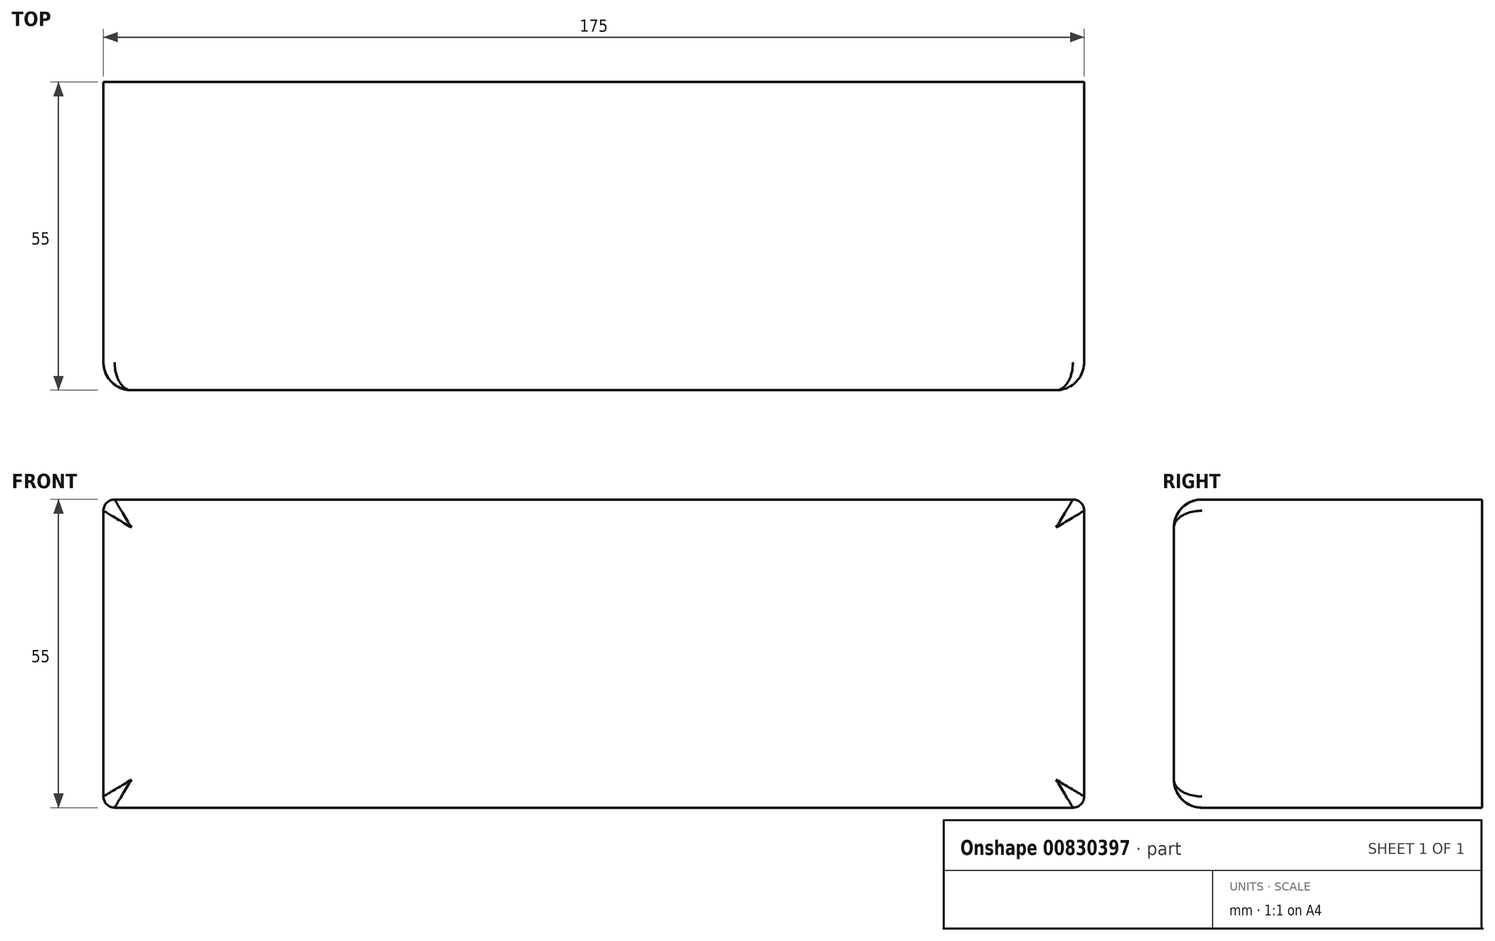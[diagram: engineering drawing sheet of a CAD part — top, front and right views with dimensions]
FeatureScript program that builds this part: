
annotation { "Feature Type Name" : "Feature", "Feature Type Description" : "" }
export const myFeature = defineFeature(function(context is Context, id is Id, definition is map)
    precondition{}
    {
        {
            var Q0;
            Q0=qCreatedBy(makeId("Front.planeOp"),FACE);
            var sketch = newSketch(context, id + "F0", { "sketchPlane" : qUnion([Q0])});
            skLineSegment(sketch, "E0.bottom", {"start": v(-82.2, 50.75) * mm, "end": v(88.8, 50.75) * mm});
            skLineSegment(sketch, "E0.top", {"start": v(-82.2, -4.25) * mm, "end": v(88.8, -4.25) * mm});
            skLineSegment(sketch, "E0.left", {"start": v(-84.2, 48.75) * mm, "end": v(-84.2, -2.25) * mm});
            skLineSegment(sketch, "E0.right", {"start": v(90.8, 48.75) * mm, "end": v(90.8, -2.25) * mm});
            skPoint(sketch, "E1.visualSharp", {"position": v(-84.2, 50.75) * mm});
            skArc(sketch, "E1.filletArc", {"start": v(-82.2, 50.75) * mm, "mid": v(-83.6, 50.16) * mm, "end": v(-84.2, 48.75) * mm});
            skPoint(sketch, "E2.visualSharp", {"position": v(-84.2, -4.25) * mm});
            skArc(sketch, "E2.filletArc", {"start": v(-84.2, -2.25) * mm, "mid": v(-83.6, -3.67) * mm, "end": v(-82.2, -4.25) * mm});
            skPoint(sketch, "E3.visualSharp", {"position": v(90.8, 50.75) * mm});
            skArc(sketch, "E3.filletArc", {"start": v(90.8, 48.75) * mm, "mid": v(90.22, 50.16) * mm, "end": v(88.8, 50.75) * mm});
            skPoint(sketch, "E4.visualSharp", {"position": v(90.8, -4.25) * mm});
            skArc(sketch, "E4.filletArc", {"start": v(88.8, -4.25) * mm, "mid": v(90.22, -3.67) * mm, "end": v(90.8, -2.25) * mm});
            skSolve(sketch);
        }
        {
            var Q0;
            Q0 = qSketchRegion(id + "F0", true);
            var Q1;
            Q1 = qSketchRegion(id + "F46LLDhD2o69u39_1", true);
            extrude(context, id + "F1", {"entities" : qUnion([Q0, Q1]), "depth" : 55 * mm, "offsetDistance" : 25 * mm});
        }
        {
            var Q0;
            Q0=makeQuery(id+"F1.opExtrude","SWEPT_EDGE",EDGE,{"disambiguationData":[OSD([sQuery(id+"F0.wireOp",EDGE,"E0.bottom"),sQuery(id+"F0.wireOp",EDGE,"E3.filletArc")])]});
            var Q1;
            Q1=makeQuery(id+"F1.opExtrude","CAP_EDGE",EDGE,{"disambiguationData":[OSD([sQuery(id+"F0.wireOp",EDGE,"E0.right")])],"isStart":false});
            fillet(context, id + "F2", {"entities" : qUnion([Q0, Q1]), "radius" : 5 * mm, "tangentPropagation" : true, "allowEdgeOverflow" : false});
        }
        {
            var Q0;
            Q0=makeQuery(id+"F1.opExtrude","CAP_FACE",FACE,{"disambiguationData":[OSD([sQuery(id+"F0.wireOp",EDGE,"E0.bottom"),sQuery(id+"F0.wireOp",EDGE,"E0.top"),sQuery(id+"F0.wireOp",EDGE,"E0.left"),sQuery(id+"F0.wireOp",EDGE,"E0.right"),sQuery(id+"F0.wireOp",EDGE,"E1.filletArc"),sQuery(id+"F0.wireOp",EDGE,"E2.filletArc"),sQuery(id+"F0.wireOp",EDGE,"E3.filletArc"),sQuery(id+"F0.wireOp",EDGE,"E4.filletArc")])],"isStart":true});
            var sketch = newSketch(context, id + "F3", { "sketchPlane" : qUnion([Q0])});
            skLineSegment(sketch, "E5.bottom", {"start": v(-85.8, 45.75) * mm, "end": v(79.2, 45.75) * mm});
            skLineSegment(sketch, "E5.top", {"start": v(-85.8, 0.75) * mm, "end": v(79.2, 0.75) * mm});
            skLineSegment(sketch, "E5.left", {"start": v(-85.8, 45.75) * mm, "end": v(-85.8, 0.75) * mm});
            skLineSegment(sketch, "E5.right", {"start": v(79.2, 45.75) * mm, "end": v(79.2, 0.75) * mm});
            skSolve(sketch);
        }
        {
            var Q0;
            Q0=makeQuery(id+"F3.imprint","IMPRINT",FACE,{"disambiguationData":[TD([[makeQuery(id+"F3.imprint","IMPRINT",EDGE,{"derivedFrom":sQuery(id+"F3.wireOp",EDGE,"E5.bottom")}),-1.0]])]});
            var Q1;
            Q1=sQuery(id+"F3.wireOp",EDGE,"E5.bottom");
            var Q2;
            Q2=sQuery(id+"F3.wireOp",EDGE,"E5.left");
            var Q3;
            Q3=sQuery(id+"F3.wireOp",EDGE,"E5.top");
            var Q4;
            Q4=sQuery(id+"F3.wireOp",EDGE,"E5.right");
            extrude(context, id + "F4", {"entities" : qUnion([Q0]), "operationType" : NewBodyOperationType.ADD, "surfaceEntities" : qUnion([Q1, Q2, Q3, Q4]), "oppositeDirection" : true, "depth" : 45 * mm, "offsetDistance" : 25 * mm});
        }
    });
